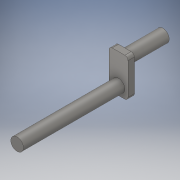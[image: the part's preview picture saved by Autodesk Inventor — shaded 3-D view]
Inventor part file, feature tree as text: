
AUTODESK INVENTOR PART (.ipt)
format: ipt  version: 2018 (Build 220112000, 112)  size: 199,680 bytes
history: native  units: in
note: dims shown in document units (in); Inventor stores cm internally (conversion verified against a paired STEP export)
features: extrude x9, sketch x9, projected_geometry x2, fillet x1
ambient origin geometry x8: Origin, YZ Plane, XZ Plane, XY Plane, X Axis, Y Axis, Z Axis, Center Point
bodies: Solid1 (feature_tree)
feature tree (21):
  extrude  "Extrusion1"  Depth=2.875in
  extrude  "Extrusion2"  Depth=2.0in
  extrude  "Extrusion3"  Depth=0.375in TaperAngle=0.0deg
  extrude  "Extrusion4"  Depth=0.125in
  extrude  "Extrusion5"  Depth=2.0in
  extrude  "Extrusion7"  Depth=0.375in TaperAngle=0.0deg
  extrude  "Extrusion6"  Depth=0.0625in
  fillet  "Fillet1"  Radius=0.375in
  extrude  "Extrusion8"  Depth=0.143in
  extrude  "Extrusion9"  Depth=2.0in TaperAngle=0.0deg
  sketch  "Sketch1"  dims[d0=0.75in d1=2.875in]
  sketch  "Sketch2"  dims[d2=0.375in d3=0.0in d4=2.0in]
  sketch  "Sketch3"  dims[d6=0.3125in d7=0.375in d8=0.0in]
  sketch  "Sketch4"  dims[d9=0.125in d10=0.3125in]
  sketch  "Sketch5"  dims[d11=0.375in d12=0.0in d13=2.0in]
  sketch  "Sketch6"  dims[d14=0.0625in d15=0.375in d16=0.0in]
  sketch  "Sketch7"  dims[d17=0.75in d18=0.0625in d19=0.375in d20=0.0in]
  sketch  "Sketch8"  dims[d21=0.25in d22=0.143in]
  projected_geometry  "Projected Loop1"
  sketch  "Sketch9"  dims[d23=0.1875in d24=2.0in d25=0.0in d26=0.25in d27=0.1875in d28=0.15in d29=0.75in d30=0.0in d31=0.0625in d32=0.75in d33=0.0in d34=2.0in d35=0.0in]
  projected_geometry  "Projected Loop2"
